# Revit family: JCI_Tyco_Union_Grv_One_Bolt_Coup_2_(DN32)_3_(DN80)
name_source: partatom
category: Pipe Fittings
units: mm (PartAtom-declared; Revit-internal decimal feet)

## family parameters
Always vertical = Yes
Cut with Voids When Loaded = No
OmniClass Number = 23.60.30.11.14
OmniClass Title = Pipework Fittings
Part Type = Union
Round Connector Dimension = Use Diameter
Shared = No
Work Plane-Based = No

## types (3) — shared parameters
COBie = Yes
COBie.Type = Yes
Description = JCI_Tyco_Union_Grv_One_Bolt_Coup_2_(DN50)_3_(DN80)
Manufacturer = Tyco Fire Protection Products
Manufacturer URL = www.tyco-fire.com
Material_ = Ductile Iron
Model = Grv One-Bolt Coup 2 (DN32) - 3 (DN80)
Technical Data Sheet No = TFP1856
zero-valued in all types: COBie.Type.NominalHeight, COBie.Type.NominalLength, COBie.Type.NominalWidth, COBie.Type.ReplacementCost, Default Elevation

## per-type parameters (varying)
| type | Finish_ |
| JCI_Tyco_Union_Grv_One_Bolt_Coup_2_(DN32)_3_(DN80) DI/Galv | Galvanized |
| JCI_Tyco_Union_Grv_One_Bolt_Coup_2_(DN32)_3_(DN80) DI/Orng | Orange |
| JCI_Tyco_Union_Grv_One_Bolt_Coup_2_(DN32)_3_(DN80) DI/Red3000 | Red |

## geometry (parser evidence)
native form markers: Sweep x103
no freeform markers — native parametric forms only
